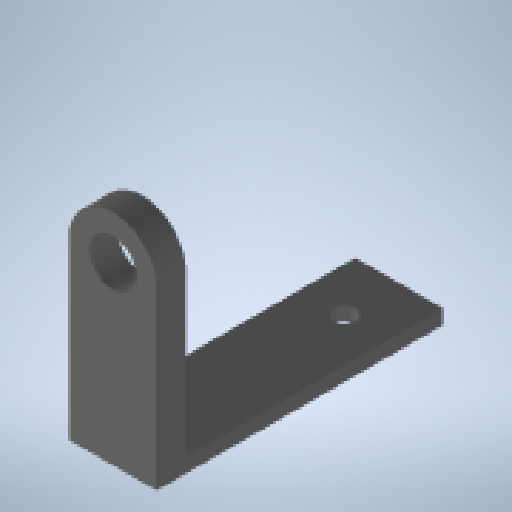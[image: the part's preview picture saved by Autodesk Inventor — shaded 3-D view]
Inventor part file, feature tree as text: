
AUTODESK INVENTOR PART (.ipt)
format: ipt  version: 2023.2 (Build 272271000, 271)  size: 185,856 bytes
history: native  units: mm
features: sketch x3, extrude x2, hole x1
ambient origin geometry x8: Origin, YZ Plane, XZ Plane, XY Plane, X Axis, Y Axis, Z Axis, Center Point
bodies: Solid1 (feature_tree)
feature tree (6):
  extrude  "Extrusion1"  Depth=15.0mm
  extrude  "Extrusion2"  Depth=15.0mm
  hole  "Hole1"  [1 undecoded]
  sketch  "Sketch1"  dims[d0=8.0mm d1=15.0mm]
  sketch  "Sketch2"  dims[d2=15.0mm d3=30.0mm]
  sketch  "Sketch3"  dims[d4=5.0mm d5=0.0mm d6=15.0mm d7=2.5mm d8=44.0mm d9=0.0mm d10=9.5mm d11=30.0mm d12=4.0mm d13=6.0mm d14=4.0mm d15=2.0mm d16=90.0deg d17=6.0mm d18=0.0mm]
note: 1 required parameter value undecoded (feature->parameter linkage not recoverable at this tier; creation-order binding heuristic only, values carry confidence <= 0.55)
